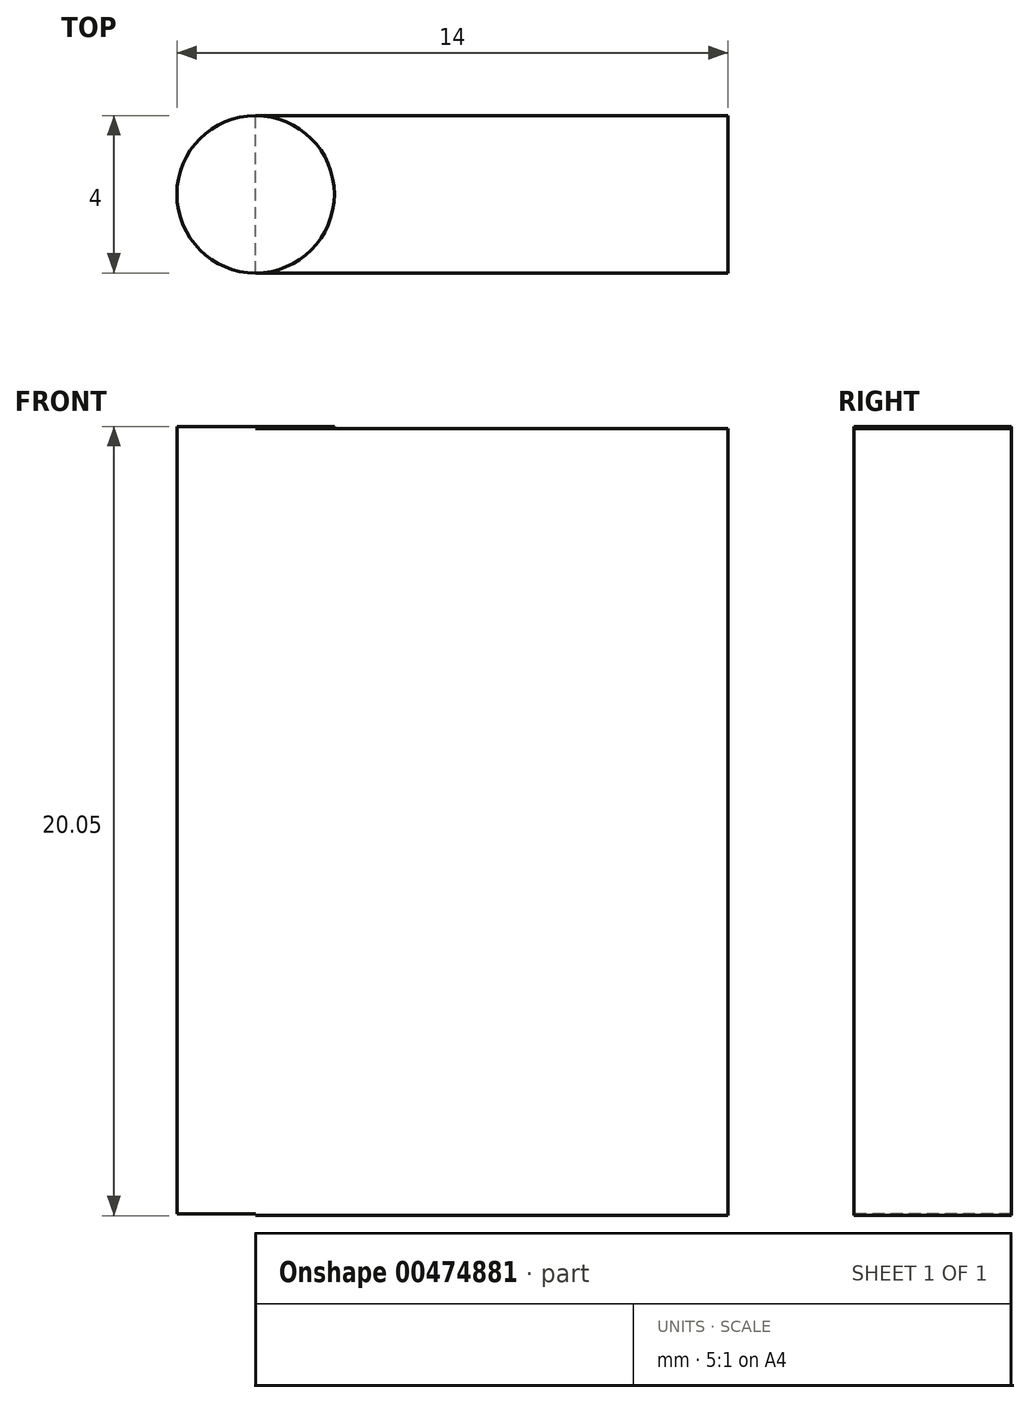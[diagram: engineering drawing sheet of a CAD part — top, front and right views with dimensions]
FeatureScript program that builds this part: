
annotation { "Feature Type Name" : "Feature", "Feature Type Description" : "" }
export const myFeature = defineFeature(function(context is Context, id is Id, definition is map)
    precondition{}
    {
        {
            var Q0;
            Q0=qCreatedBy(makeId("Top.planeOp"),FACE);
            var sketch = newSketch(context, id + "F0", { "sketchPlane" : qUnion([Q0])});
            skCircle(sketch, "E0", {"center": v(0, 0) * mm, "radius": 2 * mm});
            skSolve(sketch);
        }
        {
            var Q0;
            Q0 = qSketchRegion(id + "F0", true);
            extrude(context, id + "F1", {"entities" : qUnion([Q0]), "endBound" : BoundingType.SYMMETRIC, "depth" : 20 * mm});
        }
        {
            var Q0;
            Q0=qCreatedBy(makeId("Front.planeOp"),FACE);
            var sketch = newSketch(context, id + "F2", { "sketchPlane" : qUnion([Q0])});
            skLineSegment(sketch, "E1.bottom", {"start": v(0, 9.95) * mm, "end": v(12, 9.95) * mm});
            skLineSegment(sketch, "E1.top", {"start": v(0, -10.05) * mm, "end": v(12, -10.05) * mm});
            skLineSegment(sketch, "E1.left", {"start": v(0, 9.95) * mm, "end": v(0, -10.05) * mm});
            skLineSegment(sketch, "E1.right", {"start": v(12, 9.95) * mm, "end": v(12, -10.05) * mm});
            skSolve(sketch);
        }
        {
            var Q0;
            Q0 = qSketchRegion(id + "F2", true);
            extrude(context, id + "F3", {"entities" : qUnion([Q0]), "operationType" : NewBodyOperationType.ADD, "endBound" : BoundingType.SYMMETRIC, "depth" : 4 * mm});
        }
    });
